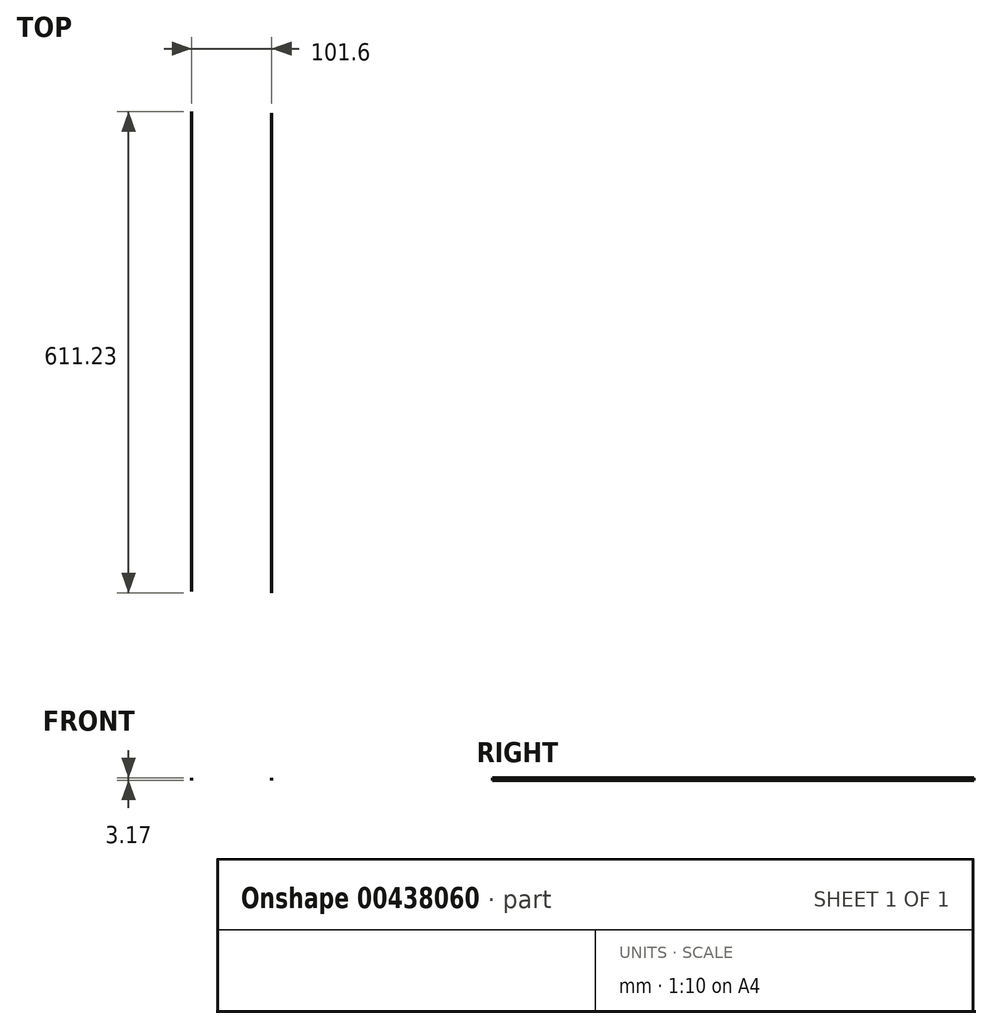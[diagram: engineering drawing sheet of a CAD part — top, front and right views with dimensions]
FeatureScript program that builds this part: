
annotation { "Feature Type Name" : "Feature", "Feature Type Description" : "" }
export const myFeature = defineFeature(function(context is Context, id is Id, definition is map)
    precondition{}
    {
        {
            var Q0;
            Q0=qCreatedBy(makeId("Top.planeOp"),FACE);
            var sketch = newSketch(context, id + "F0", { "sketchPlane" : qUnion([Q0])});
            skLineSegment(sketch, "E0", {"start": v(0, 441.72) * mm, "end": v(0, -167.88) * mm});
            skLineSegment(sketch, "E1", {"start": v(101.6, 440.09) * mm, "end": v(101.6, -169.51) * mm});
            skSolve(sketch);
        }
        {
            var Q0;
            Q0=sQuery(id+"F0.wireOp",EDGE,"E1");
            var Q1;
            Q1=sQuery(id+"F0.wireOp",EDGE,"E0");
            extrude(context, id + "F1", {"bodyType" : ToolBodyType.SURFACE, "surfaceEntities" : qUnion([Q0, Q1]), "depth" : 3.17 * mm});
        }
    });
